# Revit family: 307_5351282f38ed42f992f4f57b8bada2
name_source: partatom
category: Pipe Accessories
units: mm (PartAtom-declared; Revit-internal decimal feet)

## family parameters
Always vertical = Yes
Cut with Voids When Loaded = No
Part Type = Breaks Into
Round Connector Dimension = Use Diameter
Shared = No
Work Plane-Based = No

## types (1)
- 2895 12
    C = 11 mm  [stored 0.0360892 ft]
    C__ve = -11 mm  [stored -0.0360892 ft]
    D = 15 mm
    D2 = 8 mm  [stored 0.0262467 ft]
    D24 = 12 mm  [stored 0.0393701 ft]
    D28 = 16 mm
    DL = 27 mm
    DL2 = 26 mm
    DL5 = 23 mm  [stored 0.0754593 ft]
    Default Elevation = 0 mm  [stored 0 ft]
    Description = Water hammer arrester, ½” Male conn., max. pressure 50 bar
    HH = 46 mm  [stored 0.150919 ft]
    L2D = 53 mm  [stored 0.173885 ft]
    L2D_Min = 3048 mm  [stored 10 ft]
    MC Product Code = 2895 12
    Manufacturer = FAR
    QmdConnectorList = 301;D
    W2D = 15 mm  [stored 0.0492126 ft]
    magiPartTypeId = 307
    magiProductFamilyId = 5351282f38ed42f992f4f57b8bada2
    magiProductId = 7c6b007c90a0416182bfe3cad84858

note: [stored X ft] marks values corroborated as IEEE doubles in the binary element streams (Revit-internal decimal feet)

## geometry (parser evidence)
native form markers: Sweep x2
no freeform markers — native parametric forms only
